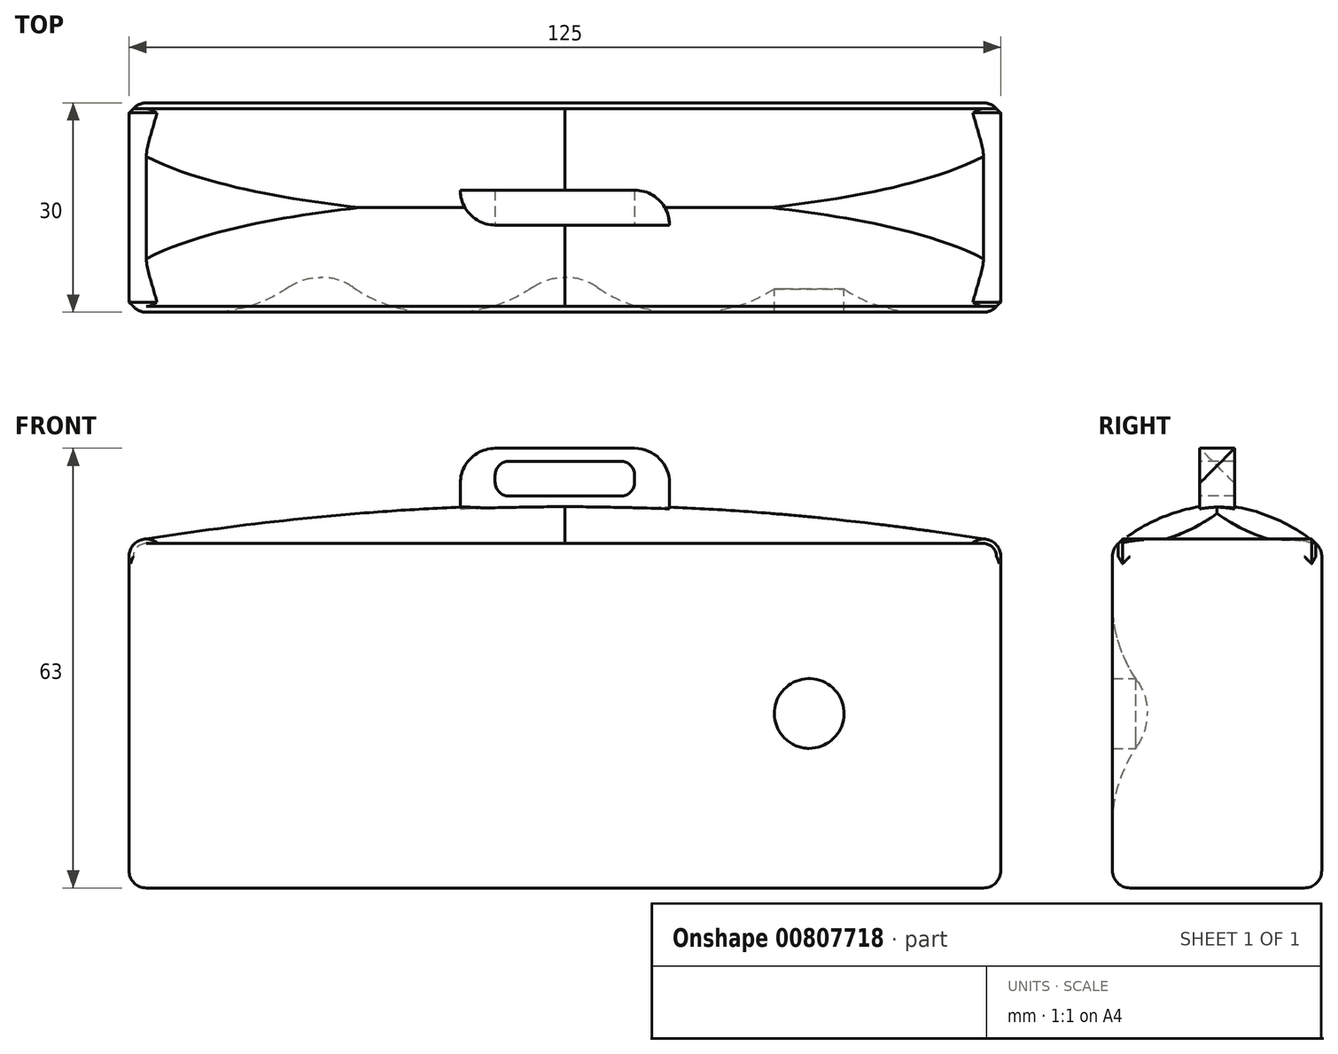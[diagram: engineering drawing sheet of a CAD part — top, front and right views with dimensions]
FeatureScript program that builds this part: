
annotation { "Feature Type Name" : "Feature", "Feature Type Description" : "" }
export const myFeature = defineFeature(function(context is Context, id is Id, definition is map)
    precondition{}
    {
        {
            var Q0;
            Q0=qCreatedBy(makeId("Front.planeOp"),FACE);
            var sketch = newSketch(context, id + "F0", { "sketchPlane" : qUnion([Q0])});
            skLineSegment(sketch, "E0.bottom", {"start": v(62.5, -25) * mm, "end": v(-62.5, -25) * mm});
            skLineSegment(sketch, "E0.top", {"start": v(62.5, 25) * mm, "end": v(-62.5, 25) * mm});
            skLineSegment(sketch, "E0.left", {"start": v(62.5, -25) * mm, "end": v(62.5, 25) * mm});
            skLineSegment(sketch, "E0.right", {"start": v(-62.5, -25) * mm, "end": v(-62.5, 25) * mm});
            skPoint(sketch, "E0.middle", {"position": v(0, 0) * mm});
            skSolve(sketch);
        }
        {
            var Q0;
            Q0=makeQuery(id+"F0.imprint","IMPRINT",FACE,{"disambiguationData":[TD([[makeQuery(id+"F0.imprint","IMPRINT",EDGE,{"derivedFrom":sQuery(id+"F0.wireOp",EDGE,"E0.bottom")}),-1.0]])]});
            extrude(context, id + "F1", {"entities" : qUnion([Q0]), "endBound" : BoundingType.SYMMETRIC, "depth" : 30 * mm, "offsetDistance" : 25 * mm});
        }
        {
            var Q0;
            Q0=makeQuery(id+"F1.opExtrude","SWEPT_EDGE",EDGE,{"disambiguationData":[OSD([sQuery(id+"F0.wireOp",EDGE,"E0.bottom"),sQuery(id+"F0.wireOp",EDGE,"E0.left")])]});
            var Q1;
            Q1=makeQuery(id+"F1.opExtrude","SWEPT_EDGE",EDGE,{"disambiguationData":[OSD([sQuery(id+"F0.wireOp",EDGE,"E0.top"),sQuery(id+"F0.wireOp",EDGE,"E0.left")])]});
            var Q2;
            Q2=makeQuery(id+"F1.opExtrude","SWEPT_EDGE",EDGE,{"disambiguationData":[OSD([sQuery(id+"F0.wireOp",EDGE,"E0.top"),sQuery(id+"F0.wireOp",EDGE,"E0.right")])]});
            var Q3;
            Q3=makeQuery(id+"F1.opExtrude","SWEPT_FACE",FACE,{"disambiguationData":[OSD([sQuery(id+"F0.wireOp",EDGE,"E0.left")])]});
            var Q4;
            Q4=makeQuery(id+"F1.opExtrude","CAP_EDGE",EDGE,{"disambiguationData":[OSD([sQuery(id+"F0.wireOp",EDGE,"E0.bottom")])],"isStart":false});
            var Q5;
            Q5=makeQuery(id+"F1.opExtrude","CAP_EDGE",EDGE,{"disambiguationData":[OSD([sQuery(id+"F0.wireOp",EDGE,"E0.left")])],"isStart":true});
            var Q6;
            Q6=makeQuery(id+"F1.opExtrude","CAP_EDGE",EDGE,{"disambiguationData":[OSD([sQuery(id+"F0.wireOp",EDGE,"E0.left")])],"isStart":false});
            var Q7;
            Q7=makeQuery(id+"F1.opExtrude","CAP_EDGE",EDGE,{"disambiguationData":[OSD([sQuery(id+"F0.wireOp",EDGE,"E0.right")])],"isStart":false});
            var Q8;
            Q8=makeQuery(id+"F1.opExtrude","SWEPT_EDGE",EDGE,{"disambiguationData":[OSD([sQuery(id+"F0.wireOp",EDGE,"E0.bottom"),sQuery(id+"F0.wireOp",EDGE,"E0.right")])]});
            var Q9;
            Q9=makeQuery(id+"F1.opExtrude","CAP_EDGE",EDGE,{"disambiguationData":[OSD([sQuery(id+"F0.wireOp",EDGE,"E0.bottom")])],"isStart":true});
            var Q10;
            Q10=makeQuery(id+"F1.opExtrude","CAP_EDGE",EDGE,{"disambiguationData":[OSD([sQuery(id+"F0.wireOp",EDGE,"E0.top")])],"isStart":true});
            var Q11;
            Q11=makeQuery(id+"F1.opExtrude","CAP_EDGE",EDGE,{"disambiguationData":[OSD([sQuery(id+"F0.wireOp",EDGE,"E0.top")])],"isStart":false});
            var Q12;
            Q12=makeQuery(id+"F1.opExtrude","CAP_EDGE",EDGE,{"disambiguationData":[OSD([sQuery(id+"F0.wireOp",EDGE,"E0.right")])],"isStart":true});
            fillet(context, id + "F2", {"entities" : qUnion([Q0, Q1, Q2, Q3, Q4, Q5, Q6, Q7, Q8, Q9, Q10, Q11, Q12]), "radius" : 2.5 * mm, "tangentPropagation" : true, "allowEdgeOverflow" : false});
        }
        {
            var Q0;
            Q0=makeQuery(id+"F1.opExtrude","CAP_FACE",FACE,{"disambiguationData":[OSD([sQuery(id+"F0.wireOp",EDGE,"E0.bottom"),sQuery(id+"F0.wireOp",EDGE,"E0.top"),sQuery(id+"F0.wireOp",EDGE,"E0.left"),sQuery(id+"F0.wireOp",EDGE,"E0.right")])],"isStart":false});
            var sketch = newSketch(context, id + "F3", { "sketchPlane" : qUnion([Q0])});
            skCircle(sketch, "E1", {"center": v(0, 0) * mm, "radius": 7.5 * mm});
            skSolve(sketch);
        }
        {
            var Q0;
            Q0 = qSketchRegion(id + "F3", true);
            extrude(context, id + "F4", {"entities" : qUnion([Q0]), "operationType" : NewBodyOperationType.REMOVE, "oppositeDirection" : true, "depth" : 5 * mm, "offsetDistance" : 25 * mm});
        }
        {
            var Q0;
            Q0=makeQuery(id+"F4.boolean.opBoolean","COPY",EDGE,{"derivedFrom":makeQuery(id+"F4.opExtrude","CAP_EDGE",EDGE,{"disambiguationData":[OSD([sQuery(id+"F3.wireOp",EDGE,"E1")])],"isStart":false})});
            fillet(context, id + "F5", {"entities" : qUnion([Q0]), "radius" : 8 * mm, "tangentPropagation" : true, "allowEdgeOverflow" : false});
        }
        {
            var Q0;
            Q0=makeQuery(id+"F1.opExtrude","CAP_FACE",FACE,{"disambiguationData":[OSD([sQuery(id+"F0.wireOp",EDGE,"E0.bottom"),sQuery(id+"F0.wireOp",EDGE,"E0.top"),sQuery(id+"F0.wireOp",EDGE,"E0.left"),sQuery(id+"F0.wireOp",EDGE,"E0.right")])],"isStart":false});
            var sketch = newSketch(context, id + "F6", { "sketchPlane" : qUnion([Q0])});
            skCircle(sketch, "E2", {"center": v(35, 0) * mm, "radius": 7.5 * mm});
            skSolve(sketch);
        }
        {
            var Q0;
            Q0=makeQuery(id+"F6.imprint","IMPRINT",FACE,{"disambiguationData":[TD([[makeQuery(id+"F6.imprint","IMPRINT",EDGE,{"derivedFrom":sQuery(id+"F6.wireOp",EDGE,"E2")}),-1.0]])]});
            var sketch = newSketch(context, id + "F7", { "sketchPlane" : qUnion([Q0])});
            skCircle(sketch, "E3", {"center": v(-35, 0) * mm, "radius": 7.5 * mm});
            skSolve(sketch);
        }
        {
            var Q0;
            Q0 = qSketchRegion(id + "F7", true);
            extrude(context, id + "F8", {"entities" : qUnion([Q0]), "operationType" : NewBodyOperationType.REMOVE, "oppositeDirection" : true, "depth" : 5 * mm, "offsetDistance" : 25 * mm});
        }
        {
            var Q0;
            Q0 = qSketchRegion(id + "F6", true);
            extrude(context, id + "F9", {"entities" : qUnion([Q0]), "operationType" : NewBodyOperationType.REMOVE, "oppositeDirection" : true, "depth" : 5 * mm, "offsetDistance" : 25 * mm});
        }
        {
            var Q0;
            Q0=makeQuery(id+"F8.boolean.opBoolean","COPY",EDGE,{"derivedFrom":makeQuery(id+"F8.opExtrude","CAP_EDGE",EDGE,{"disambiguationData":[OSD([sQuery(id+"F7.wireOp",EDGE,"E3")])],"isStart":false})});
            var Q1;
            Q1=makeQuery(id+"F9.boolean.opBoolean","COPY",EDGE,{"derivedFrom":makeQuery(id+"F9.opExtrude","CAP_EDGE",EDGE,{"disambiguationData":[OSD([sQuery(id+"F6.wireOp",EDGE,"E2")])],"isStart":false})});
            fillet(context, id + "F10", {"entities" : qUnion([Q0, Q1]), "radius" : 8 * mm, "tangentPropagation" : true, "allowEdgeOverflow" : false});
        }
        {
            var Q0;
            Q0=makeQuery(id+"F1.opExtrude","CAP_FACE",FACE,{"disambiguationData":[OSD([sQuery(id+"F0.wireOp",EDGE,"E0.bottom"),sQuery(id+"F0.wireOp",EDGE,"E0.top"),sQuery(id+"F0.wireOp",EDGE,"E0.left"),sQuery(id+"F0.wireOp",EDGE,"E0.right")])],"isStart":false});
            fillet(context, id + "F11", {"entities" : qUnion([Q0]), "radius" : 20 * mm, "tangentPropagation" : true, "allowEdgeOverflow" : false});
        }
        {
            var Q0;
            Q0=makeQuery(id+"F1.opExtrude","SWEPT_FACE",FACE,{"disambiguationData":[OSD([sQuery(id+"F0.wireOp",EDGE,"E0.top")])]});
            extrude(context, id + "F12", {"entities" : qUnion([Q0]), "operationType" : NewBodyOperationType.ADD, "depth" : 5 * mm, "offsetDistance" : 25 * mm});
        }
        {
            var Q0;
            Q0=makeQuery(id+"F12.opExtrude","CAP_EDGE",EDGE,{"disambiguationData":[OSD([sQuery(id+"F0.wireOp",EDGE,"E0.top"),sQuery(id+"F0.wireOp",EDGE,"E0.left")])],"isStart":false});
            var Q1;
            Q1=makeQuery(id+"F12.opExtrude","CAP_EDGE",EDGE,{"disambiguationData":[OSD([sQuery(id+"F0.wireOp",EDGE,"E0.top"),sQuery(id+"F0.wireOp",EDGE,"E0.right")])],"isStart":false});
            fillet(context, id + "F13", {"entities" : qUnion([Q0, Q1]), "radius" : 400 * mm, "tangentPropagation" : true, "allowEdgeOverflow" : false});
        }
        {
            var Q0;
            {var subQ0=sQuery(id+"F0.wireOp",EDGE,"E0.top");var subQ1=makeQuery(id+"F2.opFillet","BLEND_EDGE",EDGE,{"blendedFrom":[makeQuery(id+"F1.opExtrude","CAP_EDGE",EDGE,{"disambiguationData":[OSD([subQ0])],"isStart":false}),makeQuery(id+"F1.opExtrude","SWEPT_FACE",FACE,{"disambiguationData":[OSD([subQ0])]})],"blendedInto":[makeQuery(id+"F1.opExtrude","SWEPT_FACE",FACE,{"disambiguationData":[OSD([subQ0])]})]});Q0=makeQuery(id+"F12.boolean.opBoolean","MERGE",EDGE,{"derivedFrom":[subQ1,makeQuery(id+"F12.opExtrude","CAP_EDGE",EDGE,{"disambiguationData":[OSD([subQ0]),TDD([subQ1])],"isStart":true})]});}
            fillet(context, id + "F14", {"entities" : qUnion([Q0]), "radius" : 5 * mm, "tangentPropagation" : true, "allowEdgeOverflow" : false});
        }
        {
            var Q0;
            {var subQ0=sQuery(id+"F0.wireOp",EDGE,"E0.top");Q0=makeQuery(id+"F13.opFillet","BLEND_EDGE",EDGE,{"blendedFrom":[makeQuery(id+"F12.opExtrude","CAP_EDGE",EDGE,{"disambiguationData":[OSD([subQ0,sQuery(id+"F0.wireOp",EDGE,"E0.left")])],"isStart":false}),makeQuery(id+"F12.opExtrude","SWEPT_FACE",FACE,{"disambiguationData":[OSD([subQ0]),TDD([makeQuery(id+"F2.opFillet","BLEND_EDGE",EDGE,{"blendedFrom":[makeQuery(id+"F1.opExtrude","CAP_EDGE",EDGE,{"disambiguationData":[OSD([subQ0])],"isStart":false}),makeQuery(id+"F1.opExtrude","SWEPT_FACE",FACE,{"disambiguationData":[OSD([subQ0])]})],"blendedInto":[makeQuery(id+"F1.opExtrude","SWEPT_FACE",FACE,{"disambiguationData":[OSD([subQ0])]})]})])]})],"blendedInto":[makeQuery(id+"F12.opExtrude","SWEPT_FACE",FACE,{"disambiguationData":[OSD([subQ0]),TDD([makeQuery(id+"F2.opFillet","BLEND_EDGE",EDGE,{"blendedFrom":[makeQuery(id+"F1.opExtrude","CAP_EDGE",EDGE,{"disambiguationData":[OSD([subQ0])],"isStart":false}),makeQuery(id+"F1.opExtrude","SWEPT_FACE",FACE,{"disambiguationData":[OSD([subQ0])]})],"blendedInto":[makeQuery(id+"F1.opExtrude","SWEPT_FACE",FACE,{"disambiguationData":[OSD([subQ0])]})]})])]})]});}
            var Q1;
            {var subQ0=sQuery(id+"F0.wireOp",EDGE,"E0.top");Q1=makeQuery(id+"F13.opFillet","BLEND_EDGE",EDGE,{"blendedFrom":[makeQuery(id+"F12.opExtrude","CAP_EDGE",EDGE,{"disambiguationData":[OSD([subQ0,sQuery(id+"F0.wireOp",EDGE,"E0.right")])],"isStart":false}),makeQuery(id+"F12.opExtrude","SWEPT_FACE",FACE,{"disambiguationData":[OSD([subQ0]),TDD([makeQuery(id+"F2.opFillet","BLEND_EDGE",EDGE,{"blendedFrom":[makeQuery(id+"F1.opExtrude","CAP_EDGE",EDGE,{"disambiguationData":[OSD([subQ0])],"isStart":false}),makeQuery(id+"F1.opExtrude","SWEPT_FACE",FACE,{"disambiguationData":[OSD([subQ0])]})],"blendedInto":[makeQuery(id+"F1.opExtrude","SWEPT_FACE",FACE,{"disambiguationData":[OSD([subQ0])]})]})])]})],"blendedInto":[makeQuery(id+"F12.opExtrude","SWEPT_FACE",FACE,{"disambiguationData":[OSD([subQ0]),TDD([makeQuery(id+"F2.opFillet","BLEND_EDGE",EDGE,{"blendedFrom":[makeQuery(id+"F1.opExtrude","CAP_EDGE",EDGE,{"disambiguationData":[OSD([subQ0])],"isStart":false}),makeQuery(id+"F1.opExtrude","SWEPT_FACE",FACE,{"disambiguationData":[OSD([subQ0])]})],"blendedInto":[makeQuery(id+"F1.opExtrude","SWEPT_FACE",FACE,{"disambiguationData":[OSD([subQ0])]})]})])]})]});}
            var Q2;
            {var subQ0=sQuery(id+"F0.wireOp",EDGE,"E0.top");var subQ1=makeQuery(id+"F2.opFillet","BLEND_EDGE",EDGE,{"blendedFrom":[makeQuery(id+"F1.opExtrude","CAP_EDGE",EDGE,{"disambiguationData":[OSD([subQ0])],"isStart":false}),makeQuery(id+"F1.opExtrude","SWEPT_FACE",FACE,{"disambiguationData":[OSD([subQ0])]})],"blendedInto":[makeQuery(id+"F1.opExtrude","SWEPT_FACE",FACE,{"disambiguationData":[OSD([subQ0])]})]});Q2=makeQuery(id+"F14.opFillet","BLEND_EDGE",EDGE,{"blendedFrom":[makeQuery(id+"F12.boolean.opBoolean","MERGE",EDGE,{"derivedFrom":[subQ1,makeQuery(id+"F12.opExtrude","CAP_EDGE",EDGE,{"disambiguationData":[OSD([subQ0]),TDD([subQ1])],"isStart":true})]}),makeQuery(id+"F13.opFillet","BLEND_FACE",FACE,{"disambiguationData":[OSD([subQ0,sQuery(id+"F0.wireOp",EDGE,"E0.left")])]})],"blendedInto":[makeQuery(id+"F13.opFillet","BLEND_FACE",FACE,{"disambiguationData":[OSD([subQ0,sQuery(id+"F0.wireOp",EDGE,"E0.left")])]})]});}
            var Q3;
            {var subQ0=sQuery(id+"F0.wireOp",EDGE,"E0.top");var subQ1=makeQuery(id+"F2.opFillet","BLEND_EDGE",EDGE,{"blendedFrom":[makeQuery(id+"F1.opExtrude","CAP_EDGE",EDGE,{"disambiguationData":[OSD([subQ0])],"isStart":false}),makeQuery(id+"F1.opExtrude","SWEPT_FACE",FACE,{"disambiguationData":[OSD([subQ0])]})],"blendedInto":[makeQuery(id+"F1.opExtrude","SWEPT_FACE",FACE,{"disambiguationData":[OSD([subQ0])]})]});Q3=makeQuery(id+"F14.opFillet","BLEND_EDGE",EDGE,{"blendedFrom":[makeQuery(id+"F12.boolean.opBoolean","MERGE",EDGE,{"derivedFrom":[subQ1,makeQuery(id+"F12.opExtrude","CAP_EDGE",EDGE,{"disambiguationData":[OSD([subQ0]),TDD([subQ1])],"isStart":true})]}),makeQuery(id+"F13.opFillet","BLEND_FACE",FACE,{"disambiguationData":[OSD([subQ0,sQuery(id+"F0.wireOp",EDGE,"E0.right")])]})],"blendedInto":[makeQuery(id+"F13.opFillet","BLEND_FACE",FACE,{"disambiguationData":[OSD([subQ0,sQuery(id+"F0.wireOp",EDGE,"E0.right")])]})]});}
            fillet(context, id + "F15", {"entities" : qUnion([Q0, Q1, Q2, Q3]), "radius" : 25 * mm, "tangentPropagation" : true, "allowEdgeOverflow" : false});
        }
        {
            var Q0;
            {var subQ0=sQuery(id+"F0.wireOp",EDGE,"E0.top");var subQ1=makeQuery(id+"F2.opFillet","BLEND_EDGE",EDGE,{"blendedFrom":[makeQuery(id+"F1.opExtrude","CAP_EDGE",EDGE,{"disambiguationData":[OSD([subQ0])],"isStart":true}),makeQuery(id+"F1.opExtrude","SWEPT_FACE",FACE,{"disambiguationData":[OSD([subQ0])]})],"blendedInto":[makeQuery(id+"F1.opExtrude","SWEPT_FACE",FACE,{"disambiguationData":[OSD([subQ0])]})]});Q0=makeQuery(id+"F12.boolean.opBoolean","MERGE",EDGE,{"derivedFrom":[subQ1,makeQuery(id+"F12.opExtrude","CAP_EDGE",EDGE,{"disambiguationData":[OSD([subQ0]),TDD([subQ1])],"isStart":true})]});}
            fillet(context, id + "F16", {"entities" : qUnion([Q0]), "radius" : 5 * mm, "tangentPropagation" : true, "allowEdgeOverflow" : false});
        }
        {
            var Q0;
            {var subQ0=sQuery(id+"F0.wireOp",EDGE,"E0.top");Q0=makeQuery(id+"F13.opFillet","BLEND_EDGE",EDGE,{"blendedFrom":[makeQuery(id+"F12.opExtrude","CAP_EDGE",EDGE,{"disambiguationData":[OSD([subQ0,sQuery(id+"F0.wireOp",EDGE,"E0.left")])],"isStart":false}),makeQuery(id+"F12.opExtrude","SWEPT_FACE",FACE,{"disambiguationData":[OSD([subQ0]),TDD([makeQuery(id+"F2.opFillet","BLEND_EDGE",EDGE,{"blendedFrom":[makeQuery(id+"F1.opExtrude","CAP_EDGE",EDGE,{"disambiguationData":[OSD([subQ0])],"isStart":true}),makeQuery(id+"F1.opExtrude","SWEPT_FACE",FACE,{"disambiguationData":[OSD([subQ0])]})],"blendedInto":[makeQuery(id+"F1.opExtrude","SWEPT_FACE",FACE,{"disambiguationData":[OSD([subQ0])]})]})])]})],"blendedInto":[makeQuery(id+"F12.opExtrude","SWEPT_FACE",FACE,{"disambiguationData":[OSD([subQ0]),TDD([makeQuery(id+"F2.opFillet","BLEND_EDGE",EDGE,{"blendedFrom":[makeQuery(id+"F1.opExtrude","CAP_EDGE",EDGE,{"disambiguationData":[OSD([subQ0])],"isStart":true}),makeQuery(id+"F1.opExtrude","SWEPT_FACE",FACE,{"disambiguationData":[OSD([subQ0])]})],"blendedInto":[makeQuery(id+"F1.opExtrude","SWEPT_FACE",FACE,{"disambiguationData":[OSD([subQ0])]})]})])]})]});}
            var Q1;
            {var subQ0=sQuery(id+"F0.wireOp",EDGE,"E0.top");var subQ1=makeQuery(id+"F2.opFillet","BLEND_EDGE",EDGE,{"blendedFrom":[makeQuery(id+"F1.opExtrude","CAP_EDGE",EDGE,{"disambiguationData":[OSD([subQ0])],"isStart":true}),makeQuery(id+"F1.opExtrude","SWEPT_FACE",FACE,{"disambiguationData":[OSD([subQ0])]})],"blendedInto":[makeQuery(id+"F1.opExtrude","SWEPT_FACE",FACE,{"disambiguationData":[OSD([subQ0])]})]});Q1=makeQuery(id+"F16.opFillet","BLEND_EDGE",EDGE,{"blendedFrom":[makeQuery(id+"F12.boolean.opBoolean","MERGE",EDGE,{"derivedFrom":[subQ1,makeQuery(id+"F12.opExtrude","CAP_EDGE",EDGE,{"disambiguationData":[OSD([subQ0]),TDD([subQ1])],"isStart":true})]}),makeQuery(id+"F13.opFillet","BLEND_FACE",FACE,{"disambiguationData":[OSD([subQ0,sQuery(id+"F0.wireOp",EDGE,"E0.left")])]})],"blendedInto":[makeQuery(id+"F13.opFillet","BLEND_FACE",FACE,{"disambiguationData":[OSD([subQ0,sQuery(id+"F0.wireOp",EDGE,"E0.left")])]})]});}
            var Q2;
            {var subQ0=sQuery(id+"F0.wireOp",EDGE,"E0.top");Q2=makeQuery(id+"F13.opFillet","BLEND_EDGE",EDGE,{"blendedFrom":[makeQuery(id+"F12.opExtrude","CAP_EDGE",EDGE,{"disambiguationData":[OSD([subQ0,sQuery(id+"F0.wireOp",EDGE,"E0.right")])],"isStart":false}),makeQuery(id+"F12.opExtrude","SWEPT_FACE",FACE,{"disambiguationData":[OSD([subQ0]),TDD([makeQuery(id+"F2.opFillet","BLEND_EDGE",EDGE,{"blendedFrom":[makeQuery(id+"F1.opExtrude","CAP_EDGE",EDGE,{"disambiguationData":[OSD([subQ0])],"isStart":true}),makeQuery(id+"F1.opExtrude","SWEPT_FACE",FACE,{"disambiguationData":[OSD([subQ0])]})],"blendedInto":[makeQuery(id+"F1.opExtrude","SWEPT_FACE",FACE,{"disambiguationData":[OSD([subQ0])]})]})])]})],"blendedInto":[makeQuery(id+"F12.opExtrude","SWEPT_FACE",FACE,{"disambiguationData":[OSD([subQ0]),TDD([makeQuery(id+"F2.opFillet","BLEND_EDGE",EDGE,{"blendedFrom":[makeQuery(id+"F1.opExtrude","CAP_EDGE",EDGE,{"disambiguationData":[OSD([subQ0])],"isStart":true}),makeQuery(id+"F1.opExtrude","SWEPT_FACE",FACE,{"disambiguationData":[OSD([subQ0])]})],"blendedInto":[makeQuery(id+"F1.opExtrude","SWEPT_FACE",FACE,{"disambiguationData":[OSD([subQ0])]})]})])]})]});}
            var Q3;
            {var subQ0=sQuery(id+"F0.wireOp",EDGE,"E0.top");var subQ1=makeQuery(id+"F2.opFillet","BLEND_EDGE",EDGE,{"blendedFrom":[makeQuery(id+"F1.opExtrude","CAP_EDGE",EDGE,{"disambiguationData":[OSD([subQ0])],"isStart":true}),makeQuery(id+"F1.opExtrude","SWEPT_FACE",FACE,{"disambiguationData":[OSD([subQ0])]})],"blendedInto":[makeQuery(id+"F1.opExtrude","SWEPT_FACE",FACE,{"disambiguationData":[OSD([subQ0])]})]});Q3=makeQuery(id+"F16.opFillet","BLEND_EDGE",EDGE,{"blendedFrom":[makeQuery(id+"F12.boolean.opBoolean","MERGE",EDGE,{"derivedFrom":[subQ1,makeQuery(id+"F12.opExtrude","CAP_EDGE",EDGE,{"disambiguationData":[OSD([subQ0]),TDD([subQ1])],"isStart":true})]}),makeQuery(id+"F13.opFillet","BLEND_FACE",FACE,{"disambiguationData":[OSD([subQ0,sQuery(id+"F0.wireOp",EDGE,"E0.right")])]})],"blendedInto":[makeQuery(id+"F13.opFillet","BLEND_FACE",FACE,{"disambiguationData":[OSD([subQ0,sQuery(id+"F0.wireOp",EDGE,"E0.right")])]})]});}
            fillet(context, id + "F17", {"entities" : qUnion([Q0, Q1, Q2, Q3]), "radius" : 25 * mm, "tangentPropagation" : true, "allowEdgeOverflow" : false});
        }
        {
            var Q0;
            Q0=qCreatedBy(makeId("Top.planeOp"),FACE);
            var sketch = newSketch(context, id + "F18", { "sketchPlane" : qUnion([Q0])});
            skLineSegment(sketch, "E4.bottom", {"start": v(15, -2.5) * mm, "end": v(-15, -2.5) * mm});
            skLineSegment(sketch, "E4.top", {"start": v(15, 2.5) * mm, "end": v(-15, 2.5) * mm});
            skLineSegment(sketch, "E4.left", {"start": v(15, -2.5) * mm, "end": v(15, 2.5) * mm});
            skLineSegment(sketch, "E4.right", {"start": v(-15, -2.5) * mm, "end": v(-15, 2.5) * mm});
            skPoint(sketch, "E4.middle", {"position": v(0, 0) * mm});
            skSolve(sketch);
        }
        {
            var Q0;
            Q0 = qSketchRegion(id + "F18", true);
            extrude(context, id + "F19", {"entities" : qUnion([Q0]), "operationType" : NewBodyOperationType.ADD, "depth" : 38 * mm, "offsetDistance" : 25 * mm});
        }
        {
            var Q0;
            Q0=makeQuery(id+"F19.opExtrude","SWEPT_FACE",FACE,{"disambiguationData":[OSD([sQuery(id+"F18.wireOp",EDGE,"E4.bottom")])]});
            var sketch = newSketch(context, id + "F20", { "sketchPlane" : qUnion([Q0])});
            skLineSegment(sketch, "E5.bottom", {"start": v(10, 31.15) * mm, "end": v(-10, 31.15) * mm});
            skLineSegment(sketch, "E5.top", {"start": v(10, 36.15) * mm, "end": v(-10, 36.15) * mm});
            skLineSegment(sketch, "E5.left", {"start": v(10, 31.15) * mm, "end": v(10, 36.15) * mm});
            skLineSegment(sketch, "E5.right", {"start": v(-10, 31.15) * mm, "end": v(-10, 36.15) * mm});
            skPoint(sketch, "E5.middle", {"position": v(0, 33.65) * mm});
            skSolve(sketch);
        }
        {
            var Q0;
            Q0=makeQuery(id+"F20.imprint","IMPRINT",FACE,{"disambiguationData":[TD([[makeQuery(id+"F20.imprint","IMPRINT",EDGE,{"derivedFrom":sQuery(id+"F20.wireOp",EDGE,"E5.bottom")}),-1.0]])]});
            extrude(context, id + "F21", {"entities" : qUnion([Q0]), "operationType" : NewBodyOperationType.REMOVE, "oppositeDirection" : true, "depth" : 25 * mm, "offsetDistance" : 25 * mm});
        }
        {
            var Q0;
            Q0=makeQuery(id+"F21.boolean.opBoolean","COPY",EDGE,{"derivedFrom":makeQuery(id+"F21.opExtrude","SWEPT_EDGE",EDGE,{"disambiguationData":[OSD([sQuery(id+"F20.wireOp",EDGE,"E5.bottom"),sQuery(id+"F20.wireOp",EDGE,"E5.left")])]})});
            var Q1;
            Q1=makeQuery(id+"F21.boolean.opBoolean","COPY",EDGE,{"derivedFrom":makeQuery(id+"F21.opExtrude","SWEPT_EDGE",EDGE,{"disambiguationData":[OSD([sQuery(id+"F20.wireOp",EDGE,"E5.top"),sQuery(id+"F20.wireOp",EDGE,"E5.left")])]})});
            var Q2;
            Q2=makeQuery(id+"F21.boolean.opBoolean","COPY",EDGE,{"derivedFrom":makeQuery(id+"F21.opExtrude","SWEPT_EDGE",EDGE,{"disambiguationData":[OSD([sQuery(id+"F20.wireOp",EDGE,"E5.top"),sQuery(id+"F20.wireOp",EDGE,"E5.right")])]})});
            var Q3;
            Q3=makeQuery(id+"F21.boolean.opBoolean","COPY",EDGE,{"derivedFrom":makeQuery(id+"F21.opExtrude","SWEPT_EDGE",EDGE,{"disambiguationData":[OSD([sQuery(id+"F20.wireOp",EDGE,"E5.bottom"),sQuery(id+"F20.wireOp",EDGE,"E5.right")])]})});
            fillet(context, id + "F22", {"entities" : qUnion([Q0, Q1, Q2, Q3]), "radius" : 2 * mm, "tangentPropagation" : true, "allowEdgeOverflow" : false});
        }
        {
            var Q0;
            Q0=makeQuery(id+"F19.opExtrude","CAP_EDGE",EDGE,{"disambiguationData":[OSD([sQuery(id+"F18.wireOp",EDGE,"E4.right")])],"isStart":false});
            var Q1;
            Q1=makeQuery(id+"F19.opExtrude","CAP_EDGE",EDGE,{"disambiguationData":[OSD([sQuery(id+"F18.wireOp",EDGE,"E4.left")])],"isStart":false});
            var Q2;
            Q2=makeQuery(id+"F19.opExtrude","SWEPT_EDGE",EDGE,{"disambiguationData":[OSD([sQuery(id+"F18.wireOp",EDGE,"E4.top"),sQuery(id+"F18.wireOp",EDGE,"E4.left")])]});
            var Q3;
            Q3=makeQuery(id+"F19.opExtrude","SWEPT_EDGE",EDGE,{"disambiguationData":[OSD([sQuery(id+"F18.wireOp",EDGE,"E4.bottom"),sQuery(id+"F18.wireOp",EDGE,"E4.right")])]});
            fillet(context, id + "F23", {"entities" : qUnion([Q0, Q1, Q2, Q3]), "radius" : 5 * mm, "tangentPropagation" : true, "allowEdgeOverflow" : false});
        }
        {
            var Q0;
            Q0=qCreatedBy(makeId("Front.planeOp"),FACE);
            var sketch = newSketch(context, id + "F24", { "sketchPlane" : qUnion([Q0])});
            skCircle(sketch, "E6", {"center": v(35.02, 0) * mm, "radius": 5 * mm});
            skSolve(sketch);
        }
        {
            var Q0;
            Q0 = qSketchRegion(id + "F24", true);
            extrude(context, id + "F25", {"entities" : qUnion([Q0]), "operationType" : NewBodyOperationType.ADD, "depth" : 15 * mm, "offsetDistance" : 25 * mm});
        }
    });
